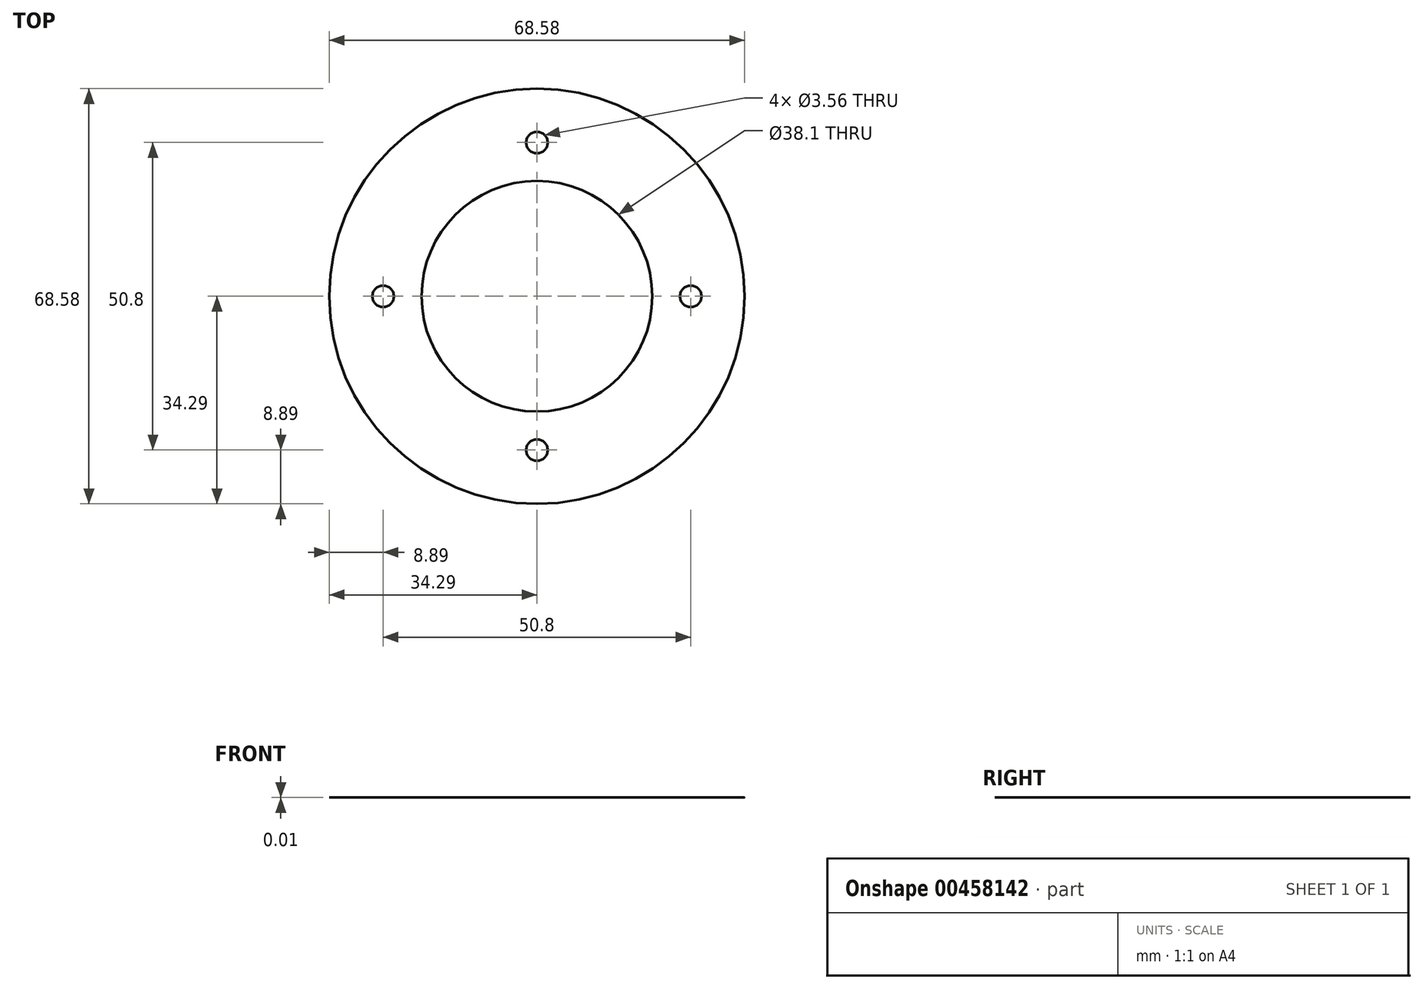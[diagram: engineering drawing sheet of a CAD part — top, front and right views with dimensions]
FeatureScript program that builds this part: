
annotation { "Feature Type Name" : "Feature", "Feature Type Description" : "" }
export const myFeature = defineFeature(function(context is Context, id is Id, definition is map)
    precondition{}
    {
        {
            var Q0;
            Q0=qCreatedBy(makeId("Top.planeOp"),FACE);
            var sketch = newSketch(context, id + "F0", { "sketchPlane" : qUnion([Q0])});
            skCircle(sketch, "E0", {"center": v(0, 0) * mm, "radius": 34.3 * mm});
            skCircle(sketch, "E1", {"center": v(0, 0) * mm, "radius": 19.05 * mm});
            skLineSegment(sketch, "E2", {"start": v(0, 0) * mm, "end": v(0, 25.4) * mm, "construction": true});
            skCircle(sketch, "E3", {"center": v(0, 25.4) * mm, "radius": 1.78 * mm});
            skCircle(sketch, "E4.1.0", {"center": v(-25.4, 0) * mm, "radius": 1.78 * mm});
            skCircle(sketch, "E4.2.0", {"center": v(0, -25.4) * mm, "radius": 1.78 * mm});
            skCircle(sketch, "E4.3.0", {"center": v(25.4, 0) * mm, "radius": 1.78 * mm});
            skSolve(sketch);
        }
        {
            var Q0;
            Q0=makeQuery(id+"F0.imprint","IMPRINT",FACE,{"disambiguationData":[TD([[makeQuery(id+"F0.imprint","IMPRINT",EDGE,{"derivedFrom":sQuery(id+"F0.wireOp",EDGE,"E0")}),1.0]])]});
            extrude(context, id + "F1", {"entities" : qUnion([Q0]), "depth" : 1 / 101.6 * mm});
        }
    });
